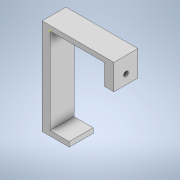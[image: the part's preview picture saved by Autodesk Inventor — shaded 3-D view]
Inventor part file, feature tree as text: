
AUTODESK INVENTOR PART (.ipt)
format: ipt  version: 2021 (Build 250183000, 183)  size: 145,408 bytes
history: native  units: mm
features: extrude x5, sketch x5, other x1
ambient origin geometry x8: Origin, YZ Plane, XZ Plane, XY Plane, X Axis, Y Axis, Z Axis, Center Point
bodies: Body1 (feature_tree)
feature tree (11):
  other  "Sólido1"
  extrude  "Extrusión1"  Depth=5.0mm
  extrude  "Extrusión2"  Depth=12.0mm TaperAngle=0.0deg
  sketch  "Boceto4"  dims[d5=60.0mm d6=0.0mm d7=12.0mm d8=0.0mm]
  extrude  "Extrusión3"  Depth=13.0mm
  extrude  "Extrusión4"  Depth=3.0mm
  extrude  "Extrusión5"  Depth=12.0mm
  sketch  "Boceto3"  dims[d2=3.0mm d3=0.0mm d4=5.0mm]
  sketch  "Boceto5"  dims[d9=13.0mm d10=7.0mm]
  sketch  "Boceto6"  dims[d11=7.5mm d12=3.0mm]
  sketch  "Boceto7"  dims[d13=3.0mm d14=0.0mm d15=12.0mm d16=7.0mm d17=6.0mm d18=3.0mm d19=6.0mm d20=0.0mm]
